# Revit family: FU_Modular_Sandler_Ambit 1060
name_source: partatom
category: Furniture
units: mm (PartAtom-declared; Revit-internal decimal feet)

## family parameters
Always vertical = Yes
Cut with Voids When Loaded = No
OmniClass Number = 23.40.20.00
OmniClass Title = General Furniture and Specialties
Room Calculation Point = No
Shared = No
Work Plane-Based = No

## types (1)
- Ambit 1060
    Default Elevation = 0 mm  [stored 0 ft]
    Depth = 700 mm  [stored 2.29659 ft]
    Description = Modular seating system. Upholstered seat and back, with feet in cast aluminium.
    Height = 770 mm  [stored 2.52625 ft]
    Manufacturer = Sandler
    Model = Ambit 1060
    Seat Type = Ambit Seat : Seat 1200mm
    URL = https://www.sandlerseating.com
    Width = 1200 mm

note: [stored X ft] marks values corroborated as IEEE doubles in the binary element streams (Revit-internal decimal feet)

## geometry (parser evidence)
native form markers: Sweep x10
no freeform markers — native parametric forms only
